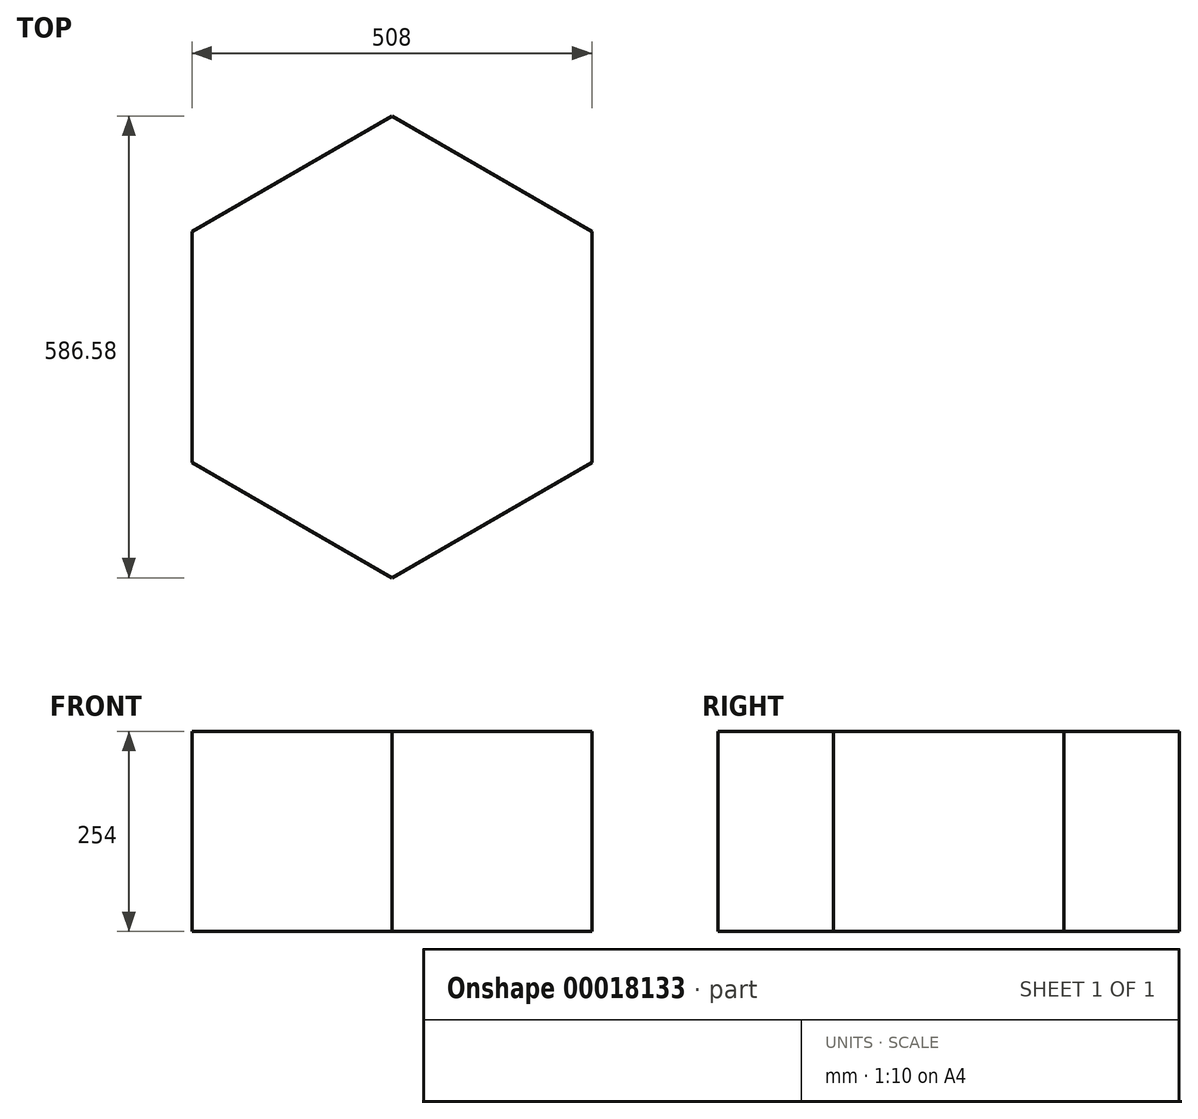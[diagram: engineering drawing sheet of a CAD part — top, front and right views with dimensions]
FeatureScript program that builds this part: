
annotation { "Feature Type Name" : "Feature", "Feature Type Description" : "" }
export const myFeature = defineFeature(function(context is Context, id is Id, definition is map)
    precondition{}
    {
        {
            var Q0;
            Q0=qCreatedBy(makeId("Top.planeOp"),FACE);
            var sketch = newSketch(context, id + "F0", { "sketchPlane" : qUnion([Q0])});
            skCircle(sketch, "E0.cCircle", {"center": v(0, 0) * mm, "radius": 293.3 * mm, "construction": true});
            skLineSegment(sketch, "E0.0", {"start": v(254, 146.65) * mm, "end": v(254, -146.65) * mm});
            skLineSegment(sketch, "E0.1", {"start": v(254, -146.65) * mm, "end": v(0, -293.3) * mm});
            skLineSegment(sketch, "E0.2", {"start": v(0, -293.3) * mm, "end": v(-254, -146.65) * mm});
            skLineSegment(sketch, "E0.3", {"start": v(-254, -146.65) * mm, "end": v(-254, 146.65) * mm});
            skLineSegment(sketch, "E0.4", {"start": v(-254, 146.65) * mm, "end": v(0, 293.3) * mm});
            skLineSegment(sketch, "E0.5", {"start": v(0, 293.3) * mm, "end": v(254, 146.65) * mm});
            skSolve(sketch);
        }
        {
            var Q0;
            Q0 = qSketchRegion(id + "F0", true);
            extrude(context, id + "F1", {"entities" : qUnion([Q0]), "endBound" : BoundingType.SYMMETRIC, "depth" : 254 * mm});
        }
        {
            var Q0;
            Q0=qCreatedBy(makeId("Front.planeOp"),FACE);
            var sketch = newSketch(context, id + "F2", { "sketchPlane" : qUnion([Q0])});
            skLineSegment(sketch, "E1", {"start": v(-203.2, 127) * mm, "end": v(-254, 76.2) * mm});
            skLineSegment(sketch, "E2", {"start": v(-254, 76.2) * mm, "end": v(-254, 127) * mm});
            skLineSegment(sketch, "E3", {"start": v(-254, 127) * mm, "end": v(-203.2, 127) * mm});
            skLineSegment(sketch, "E4", {"start": v(0, 0) * mm, "end": v(292.91, 0) * mm, "construction": true});
            skLineSegment(sketch, "E5.MirrorCS", {"start": v(-203.2, -127) * mm, "end": v(-254, -76.2) * mm});
            skLineSegment(sketch, "E6.MirrorCS", {"start": v(-254, -76.2) * mm, "end": v(-254, -127) * mm});
            skLineSegment(sketch, "E7.MirrorCS", {"start": v(-254, -127) * mm, "end": v(-203.2, -127) * mm});
            skLineSegment(sketch, "E8", {"start": v(0, 0) * mm, "end": v(0, 209.62) * mm, "construction": true});
            skSolve(sketch);
        }
        {
            var Q0;
            Q0 = qSketchRegion(id + "F2", true);
            var Q1;
            Q1=sQuery(id+"F2.wireOp",EDGE,"E8");
            revolve(context, id + "F3", {"operationType" : NewBodyOperationType.ADD, "entities" : qUnion([Q0]), "axis" : qUnion([Q1]), "revolveType" : RevolveType.FULL});
        }
    });
